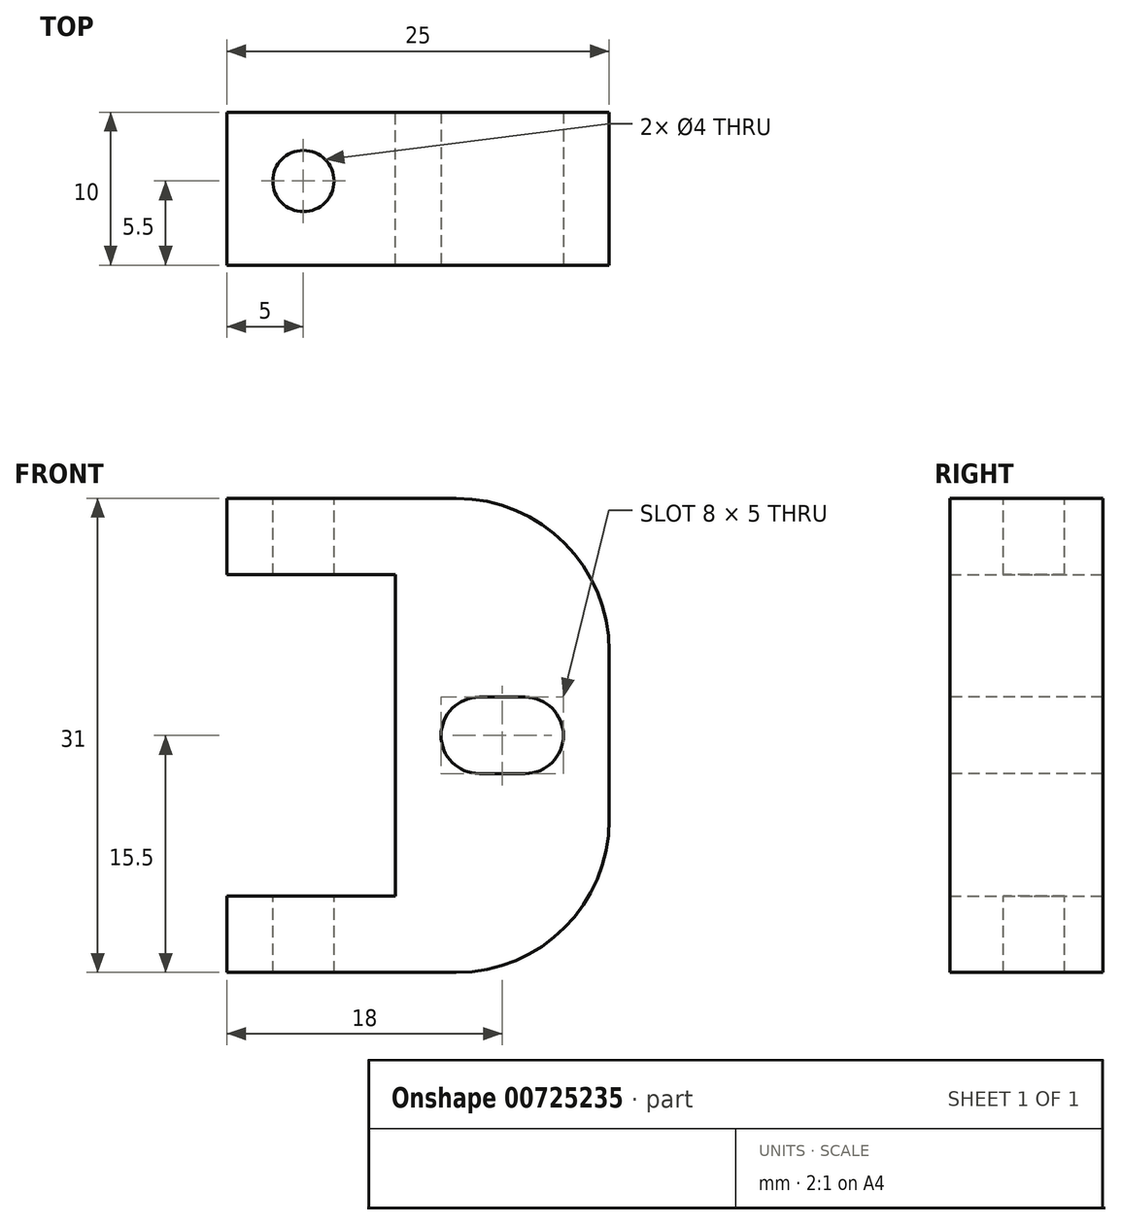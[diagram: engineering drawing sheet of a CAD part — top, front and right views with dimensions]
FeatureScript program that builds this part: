
annotation { "Feature Type Name" : "Feature", "Feature Type Description" : "" }
export const myFeature = defineFeature(function(context is Context, id is Id, definition is map)
    precondition{}
    {
        {
            var Q0;
            Q0=qCreatedBy(makeId("Top.planeOp"),FACE);
            var sketch = newSketch(context, id + "F0", { "sketchPlane" : qUnion([Q0])});
            skLineSegment(sketch, "E0.bottom", {"start": v(0, 0) * mm, "end": v(25, 0) * mm});
            skLineSegment(sketch, "E0.top", {"start": v(0, 10) * mm, "end": v(25, 10) * mm});
            skLineSegment(sketch, "E0.left", {"start": v(0, 0) * mm, "end": v(0, 10) * mm});
            skLineSegment(sketch, "E0.right", {"start": v(25, 0) * mm, "end": v(25, 10) * mm});
            skSolve(sketch);
        }
        {
            var Q0;
            Q0=makeQuery(id+"F0.imprint","IMPRINT",FACE,{"disambiguationData":[TD([[makeQuery(id+"F0.imprint","IMPRINT",EDGE,{"derivedFrom":sQuery(id+"F0.wireOp",EDGE,"E0.bottom")}),1.0]])]});
            extrude(context, id + "F1", {"entities" : qUnion([Q0]), "endBound" : BoundingType.SYMMETRIC, "depth" : 31 * mm, "offsetDistance" : 25 * mm});
        }
        {
            var Q0;
            Q0=makeQuery(id+"F1.opExtrude","SWEPT_FACE",FACE,{"disambiguationData":[OSD([sQuery(id+"F0.wireOp",EDGE,"E0.top")])]});
            var sketch = newSketch(context, id + "F2", { "sketchPlane" : qUnion([Q0])});
            skLineSegment(sketch, "E1.bottom", {"start": v(0, -10.5) * mm, "end": v(-11, -10.5) * mm});
            skLineSegment(sketch, "E1.top", {"start": v(0, 10.5) * mm, "end": v(-11, 10.5) * mm});
            skLineSegment(sketch, "E1.left", {"start": v(0, -10.5) * mm, "end": v(0, 10.5) * mm});
            skLineSegment(sketch, "E1.right", {"start": v(-11, -10.5) * mm, "end": v(-11, 10.5) * mm});
            skSolve(sketch);
        }
        {
            var Q0;
            Q0=makeQuery(id+"F2.imprint","IMPRINT",FACE,{"disambiguationData":[TD([[makeQuery(id+"F2.imprint","IMPRINT",EDGE,{"derivedFrom":sQuery(id+"F2.wireOp",EDGE,"E1.bottom")}),-1.0]])]});
            extrude(context, id + "F3", {"entities" : qUnion([Q0]), "operationType" : NewBodyOperationType.REMOVE, "endBound" : BoundingType.THROUGH_ALL, "oppositeDirection" : true, "depth" : 25 * mm, "offsetDistance" : 25 * mm});
        }
        {
            var Q0;
            Q0=makeQuery(id+"F1.opExtrude","SWEPT_FACE",FACE,{"disambiguationData":[OSD([sQuery(id+"F0.wireOp",EDGE,"E0.top")])]});
            var sketch = newSketch(context, id + "F4", { "sketchPlane" : qUnion([Q0])});
            skLineSegment(sketch, "E2", {"start": v(-11, 0) * mm, "end": v(-25, 0) * mm, "construction": true});
            skPoint(sketch, "E3", {"position": v(-18, 0) * mm});
            skCircle(sketch, "E4", {"center": v(-18, 0) * mm, "radius": 2.5 * mm});
            skSolve(sketch);
        }
        {
            var Q0;
            Q0 = qSketchRegion(id + "F4", true);
            extrude(context, id + "F5", {"entities" : qUnion([Q0]), "operationType" : NewBodyOperationType.REMOVE, "endBound" : BoundingType.THROUGH_ALL, "oppositeDirection" : true, "depth" : 25 * mm, "offsetDistance" : 25 * mm});
        }
        {
            var Q0;
            Q0=makeQuery(id+"F1.opExtrude","CAP_EDGE",EDGE,{"disambiguationData":[OSD([sQuery(id+"F0.wireOp",EDGE,"E0.right")])],"isStart":true});
            var Q1;
            Q1=makeQuery(id+"F1.opExtrude","CAP_EDGE",EDGE,{"disambiguationData":[OSD([sQuery(id+"F0.wireOp",EDGE,"E0.right")])],"isStart":false});
            fillet(context, id + "F6", {"entities" : qUnion([Q0, Q1]), "radius" : 10 * mm, "tangentPropagation" : true, "allowEdgeOverflow" : false});
        }
        {
            var Q0;
            Q0=qCreatedBy(makeId("Top.planeOp"),FACE);
            var sketch = newSketch(context, id + "F7", { "sketchPlane" : qUnion([Q0])});
            skPoint(sketch, "E5", {"position": v(5, 5.5) * mm});
            skCircle(sketch, "E6", {"center": v(5, 5.5) * mm, "radius": 2 * mm});
            skSolve(sketch);
        }
        {
            var Q0;
            Q0 = qSketchRegion(id + "F7", true);
            extrude(context, id + "F8", {"entities" : qUnion([Q0]), "operationType" : NewBodyOperationType.REMOVE, "endBound" : BoundingType.SYMMETRIC, "oppositeDirection" : true, "depth" : 32 * mm, "offsetDistance" : 25 * mm});
        }
        {
            var Q0;
            Q0=makeQuery(id+"F1.opExtrude","SWEPT_FACE",FACE,{"disambiguationData":[OSD([sQuery(id+"F0.wireOp",EDGE,"E0.bottom")])]});
            var sketch = newSketch(context, id + "F9", { "sketchPlane" : qUnion([Q0])});
            skLineSegment(sketch, "E7.bottom", {"start": v(16.5, 2.5) * mm, "end": v(19.5, 2.5) * mm});
            skLineSegment(sketch, "E7.top", {"start": v(16.5, -2.5) * mm, "end": v(19.5, -2.5) * mm});
            skLineSegment(sketch, "E7.left", {"start": v(16.5, 2.5) * mm, "end": v(16.5, -2.5) * mm, "construction": true});
            skLineSegment(sketch, "E7.right", {"start": v(19.5, 2.5) * mm, "end": v(19.5, -2.5) * mm, "construction": true});
            skPoint(sketch, "E7.middle", {"position": v(18, 0) * mm});
            skArc(sketch, "E8", {"start": v(16.5, 2.5) * mm, "mid": v(14, 0) * mm, "end": v(16.5, -2.5) * mm});
            skArc(sketch, "E9", {"start": v(19.5, -2.5) * mm, "mid": v(22, 0) * mm, "end": v(19.5, 2.5) * mm});
            skSolve(sketch);
        }
        {
            var Q0;
            Q0 = qSketchRegion(id + "F9", true);
            extrude(context, id + "F10", {"entities" : qUnion([Q0]), "operationType" : NewBodyOperationType.REMOVE, "oppositeDirection" : true, "depth" : 25 * mm, "offsetDistance" : 25 * mm});
        }
    });
